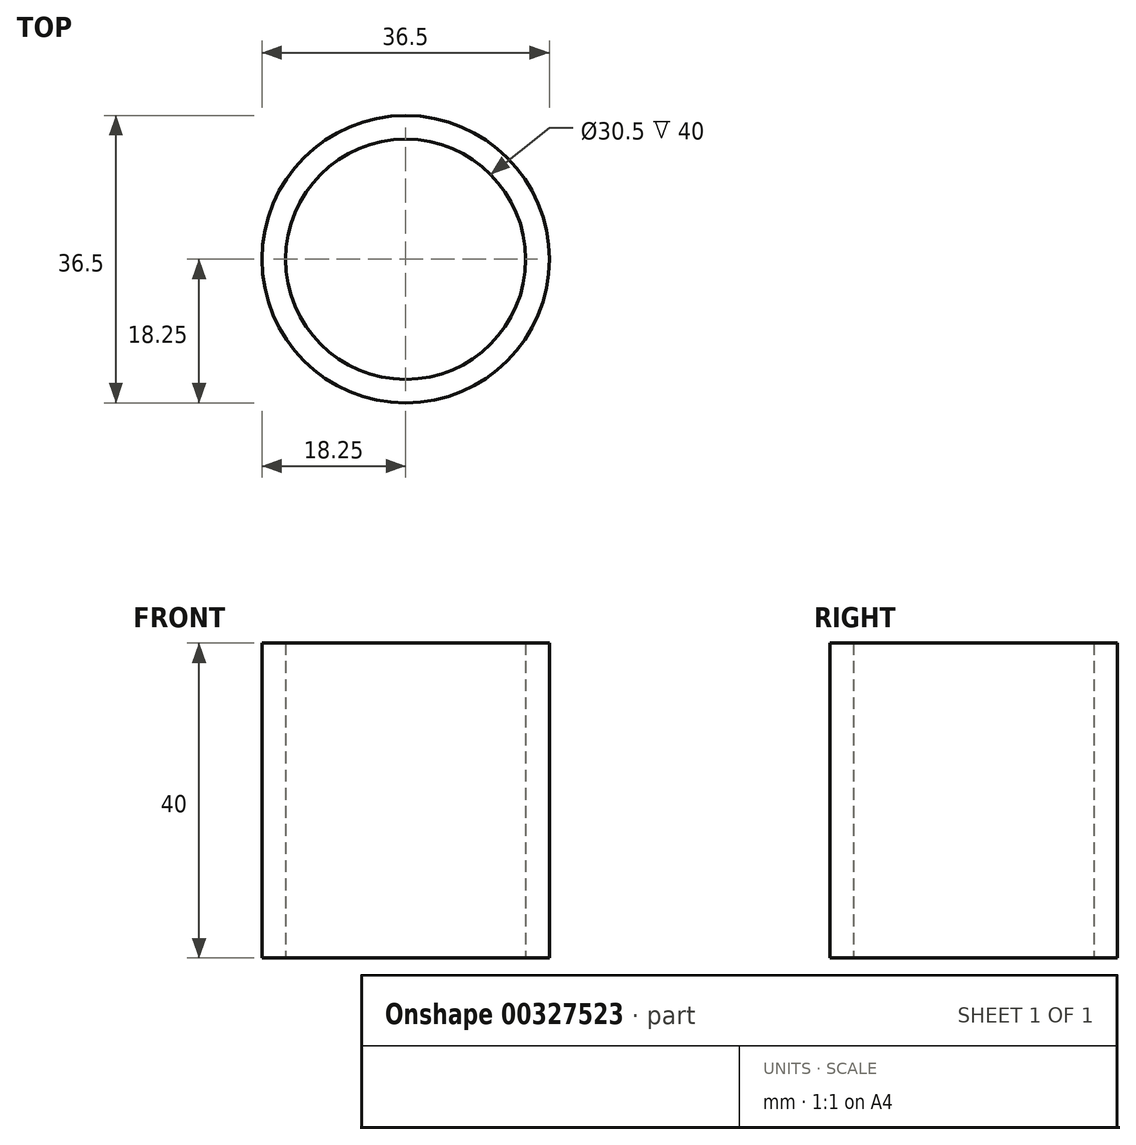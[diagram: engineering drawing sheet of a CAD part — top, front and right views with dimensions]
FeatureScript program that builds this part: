
annotation { "Feature Type Name" : "Feature", "Feature Type Description" : "" }
export const myFeature = defineFeature(function(context is Context, id is Id, definition is map)
    precondition{}
    {
        {
            var Q0;
            Q0=qCreatedBy(makeId("Top.planeOp"),FACE);
            var sketch = newSketch(context, id + "F0", { "sketchPlane" : qUnion([Q0])});
            skCircle(sketch, "E0", {"center": v(0, 0) * mm, "radius": 15.25 * mm});
            skCircle(sketch, "E1", {"center": v(0, 0) * mm, "radius": 18.25 * mm});
            skCircle(sketch, "E2", {"center": v(0, 0) * mm, "radius": 24.6 * mm, "construction": true});
            skSolve(sketch);
        }
        {
            var Q0;
            Q0 = qSketchRegion(id + "F0", true);
            var Q1;
            Q1=sQuery(id+"F0.wireOp",EDGE,"E1");
            var Q2;
            Q2=sQuery(id+"F0.wireOp",EDGE,"E0");
            extrude(context, id + "F1", {"entities" : qUnion([Q0]), "surfaceEntities" : qUnion([Q1, Q2]), "depth" : 40 * mm, "symmetric" : true});
        }
    });
